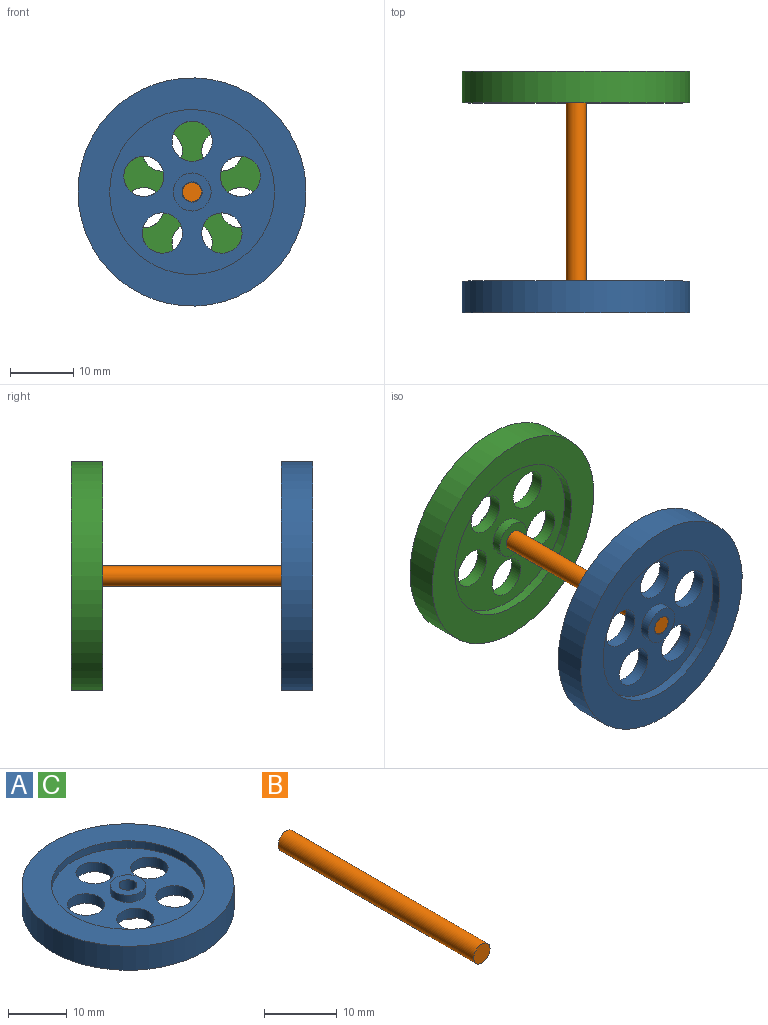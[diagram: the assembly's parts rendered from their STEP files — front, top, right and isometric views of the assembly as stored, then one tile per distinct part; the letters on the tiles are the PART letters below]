
ASSEMBLY  parts=3 mates=1
PART A: 17 faces, bbox 36x36x5 mm
  f0: cylinder r=18mm len=36mm, axis (0,0,-1), area 565.5mm2, adj f1,f10
  f1: plane 36x36mm, normal (0,0,1), area 486.9mm2, adj f0,f2
  f2: cylinder r=13mm len=26mm, axis (0,0,-1), area 122.5mm2, adj f1,f3
  f3: plane 26x26mm, normal (0,0,1), area 344.3mm2, adj f2,f4,f12,f13,f14,f15,f16
  f4: cylinder r=3mm len=6mm, axis (0,0,-1), area 28.3mm2, adj f3,f5
  f5: plane 6x6mm, normal (0,0,1), area 21.2mm2, adj f4,f11
  f6: plane 6x6mm, normal (0,0,-1), area 21.2mm2, adj f7,f11
  f7: cylinder r=3mm len=6mm, axis (0,0,-1), area 28.3mm2, adj f6,f8
  f8: plane 26x26mm, normal (0,0,-1), area 344.3mm2, adj f7,f9,f12,f13,f14,f15,f16
  f9: cylinder r=13mm len=26mm, axis (0,0,-1), area 122.5mm2, adj f8,f10
  f10: plane 36x36mm, normal (0,0,-1), area 486.9mm2, adj f0,f9
  f11: cylinder r=1.5mm len=5mm, axis (0,0,-1), area 47.1mm2, adj f5,f6
  f12: cylinder r=3.17mm len=6.35mm, axis (0,0,1), area 39.9mm2, adj f3,f8
  f13: cylinder r=3.17mm len=6.35mm, axis (0,0,1), area 39.9mm2, adj f3,f8
  f14: cylinder r=3.17mm len=6.35mm, axis (0,0,1), area 39.9mm2, adj f3,f8
  f15: cylinder r=3.17mm len=6.35mm, axis (0,0,1), area 39.9mm2, adj f3,f8
  f16: cylinder r=3.17mm len=6.35mm, axis (0,0,1), area 39.9mm2, adj f3,f8
PART B: 3 faces, bbox 3.2x38.1x3.2 mm
  f0: cylinder r=1.59mm len=38.1mm, axis (0,1,0), area 380mm2, adj f1,f2
  f1: plane 3.18x3.18mm, normal (0,-1,0), area 7.9mm2, adj f0
  f2: plane 3.18x3.18mm, normal (0,1,0), area 7.9mm2, adj f0
PART C: same geometry as A
PLACE A rot(axis=(1,0,0),90deg) t=(-32.99,-46.09,-8.09)mm
PLACE B t=(-8.82,-10.49,-8.09)mm fixed
PLACE C rot(axis=(-1,0,0),90deg) t=(-32.99,-12.99,-8.09)mm
MATE fastened C.f0 <-> B.f0  axis (0,1,0) through (-32.99,-10.49,-8.09)mm
